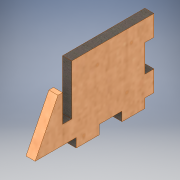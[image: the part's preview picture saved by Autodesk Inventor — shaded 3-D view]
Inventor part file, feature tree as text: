
AUTODESK INVENTOR PART (.ipt)
format: ipt  version: 2019 (Build 230136000, 136)  size: 149,504 bytes
history: native  units: mm
features: other x1, extrude x1, sketch x1
ambient origin geometry x8: Origin, YZ Plane, XZ Plane, XY Plane, X Axis, Y Axis, Z Axis, Center Point
bodies: Body1 (feature_tree)
feature tree (3):
  other  "Твердое тело1"
  extrude  "Выдавливание1"  Depth=30.0mm
  sketch  "Эскиз1"
